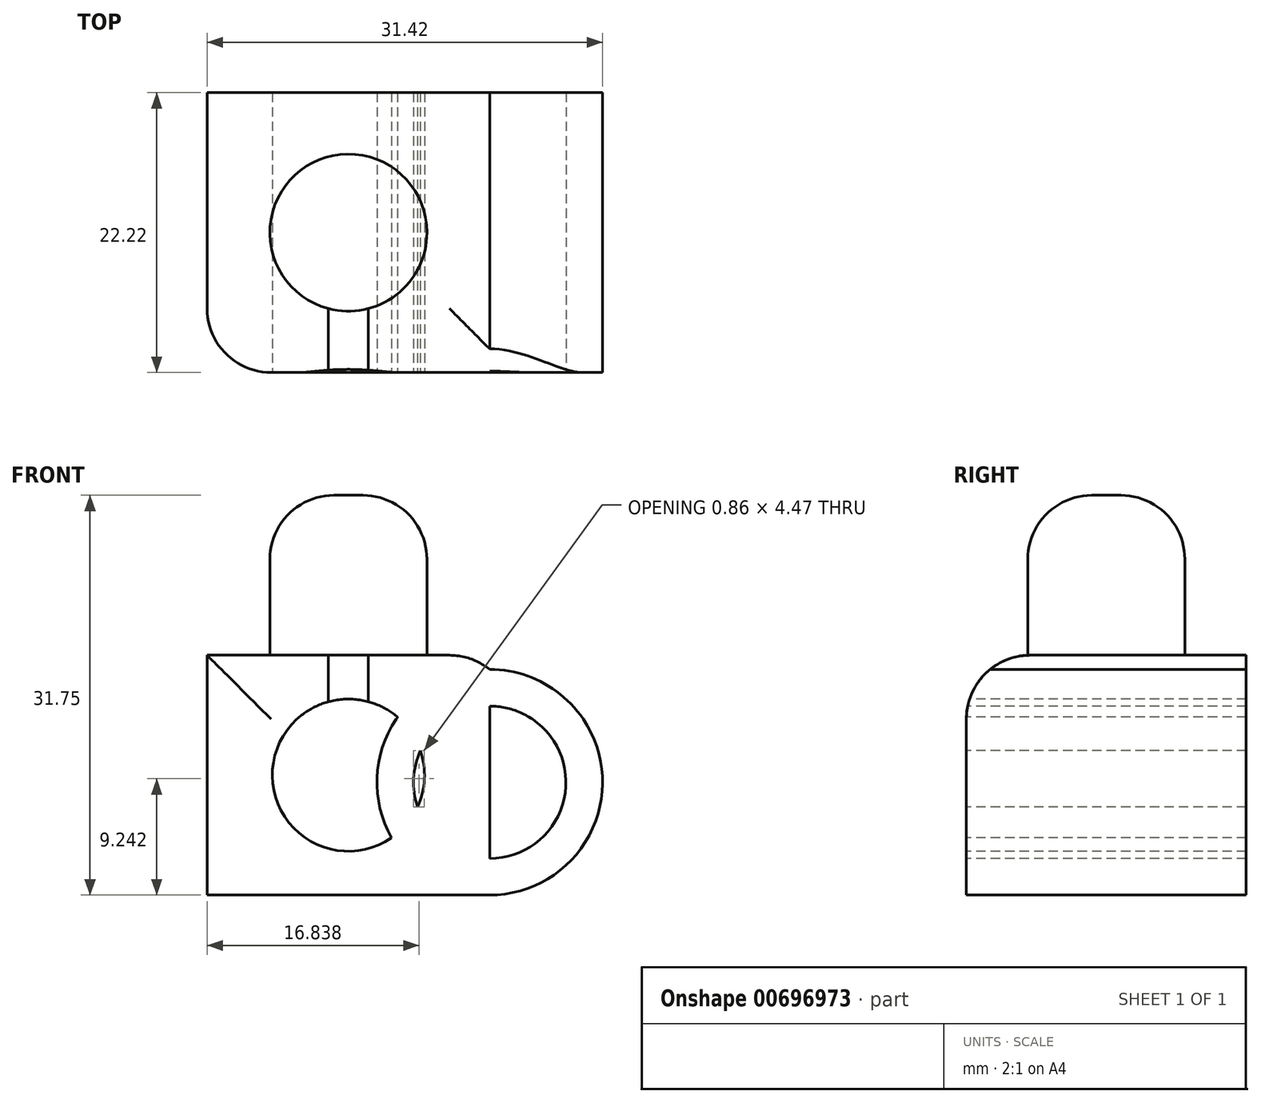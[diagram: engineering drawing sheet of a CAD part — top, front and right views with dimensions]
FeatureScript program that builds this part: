
annotation { "Feature Type Name" : "Feature", "Feature Type Description" : "" }
export const myFeature = defineFeature(function(context is Context, id is Id, definition is map)
    precondition{}
    {
        {
            var Q0;
            Q0=qCreatedBy(makeId("Top.planeOp"),FACE);
            var sketch = newSketch(context, id + "F0", { "sketchPlane" : qUnion([Q0])});
            skLineSegment(sketch, "E0.bottom", {"start": v(11.23, -11.11) * mm, "end": v(-11.23, -11.11) * mm});
            skLineSegment(sketch, "E0.top", {"start": v(11.23, 11.11) * mm, "end": v(-11.23, 11.11) * mm});
            skLineSegment(sketch, "E0.left", {"start": v(11.23, -11.11) * mm, "end": v(11.23, 11.11) * mm});
            skLineSegment(sketch, "E0.right", {"start": v(-11.23, -11.11) * mm, "end": v(-11.23, 11.11) * mm});
            skPoint(sketch, "E0.middle", {"position": v(0, 0) * mm});
            skSolve(sketch);
        }
        {
            var Q0;
            Q0=makeQuery(id+"F0.imprint","IMPRINT",FACE,{"disambiguationData":[TD([[makeQuery(id+"F0.imprint","IMPRINT",EDGE,{"derivedFrom":sQuery(id+"F0.wireOp",EDGE,"E0.bottom")}),-1.0]])]});
            extrude(context, id + "F1", {"entities" : qUnion([Q0]), "depth" : 19.05 * mm, "offsetDistance" : 25.4 * mm});
        }
        {
            var Q0;
            Q0=makeQuery(id+"F1.opExtrude","CAP_FACE",FACE,{"disambiguationData":[OSD([sQuery(id+"F0.wireOp",EDGE,"E0.bottom"),sQuery(id+"F0.wireOp",EDGE,"E0.top"),sQuery(id+"F0.wireOp",EDGE,"E0.left"),sQuery(id+"F0.wireOp",EDGE,"E0.right")])],"isStart":false});
            var sketch = newSketch(context, id + "F2", { "sketchPlane" : qUnion([Q0])});
            skCircle(sketch, "E1", {"center": v(0, 0) * mm, "radius": 6.24 * mm});
            skSolve(sketch);
        }
        {
            var Q0;
            Q0=makeQuery(id+"F2.imprint","IMPRINT",FACE,{"disambiguationData":[TD([[makeQuery(id+"F2.imprint","IMPRINT",EDGE,{"derivedFrom":sQuery(id+"F2.wireOp",EDGE,"E1")}),1.0]])]});
            extrude(context, id + "F3", {"entities" : qUnion([Q0]), "operationType" : NewBodyOperationType.ADD, "depth" : 12.7 * mm, "offsetDistance" : 25.4 * mm});
        }
        {
            var Q0;
            Q0=makeQuery(id+"F1.opExtrude","SWEPT_FACE",FACE,{"disambiguationData":[OSD([sQuery(id+"F0.wireOp",EDGE,"E0.bottom")])]});
            var sketch = newSketch(context, id + "F4", { "sketchPlane" : qUnion([Q0])});
            skCircle(sketch, "E2", {"center": v(0, 9.53) * mm, "radius": 6.04 * mm});
            skPoint(sketch, "E2.centerSnap0", {"position": v(-11.23, 9.53) * mm});
            skSolve(sketch);
        }
        {
            var Q0;
            Q0=makeQuery(id+"F4.imprint","IMPRINT",FACE,{"disambiguationData":[TD([[makeQuery(id+"F4.imprint","IMPRINT",EDGE,{"derivedFrom":sQuery(id+"F4.wireOp",EDGE,"E2")}),1.0]])]});
            extrude(context, id + "F5", {"entities" : qUnion([Q0]), "operationType" : NewBodyOperationType.REMOVE, "oppositeDirection" : true, "depth" : 25.4 * mm, "offsetDistance" : 25.4 * mm});
        }
        {
            var Q0;
            Q0=makeQuery(id+"F1.opExtrude","SWEPT_FACE",FACE,{"disambiguationData":[OSD([sQuery(id+"F0.wireOp",EDGE,"E0.left")])]});
            var sketch = newSketch(context, id + "F6", { "sketchPlane" : qUnion([Q0])});
            skLineSegment(sketch, "E3.bottom", {"start": v(11.11, 0) * mm, "end": v(-11.11, 0) * mm});
            skLineSegment(sketch, "E3.top", {"start": v(11.11, 2.9) * mm, "end": v(-11.11, 2.9) * mm});
            skLineSegment(sketch, "E3.left", {"start": v(11.11, 0) * mm, "end": v(11.11, 2.9) * mm});
            skLineSegment(sketch, "E3.right", {"start": v(-11.11, 0) * mm, "end": v(-11.11, 2.9) * mm});
            skPoint(sketch, "E3.middle", {"position": v(0, 1.45) * mm});
            skLineSegment(sketch, "E4", {"start": v(-11.11, 8.96) * mm, "end": v(11.11, 8.96) * mm});
            skSolve(sketch);
        }
        {
            var Q0;
            Q0=makeQuery(id+"F6.imprint","IMPRINT",FACE,{"disambiguationData":[TD([[makeQuery(id+"F6.imprint","IMPRINT",EDGE,{"derivedFrom":sQuery(id+"F6.wireOp",EDGE,"E3.bottom")}),1.0]])]});
            var Q1;
            Q1=sQuery(id+"F6.wireOp",EDGE,"E4");
            revolve(context, id + "F7", {"operationType" : NewBodyOperationType.ADD, "entities" : qUnion([Q0]), "axis" : qUnion([Q1]), "revolveType" : RevolveType.FULL});
        }
        {
            var Q0;
            Q0=makeQuery(id+"F1.opExtrude","CAP_EDGE",EDGE,{"disambiguationData":[OSD([sQuery(id+"F0.wireOp",EDGE,"E0.bottom")])],"isStart":false});
            var Q1;
            Q1=makeQuery(id+"F1.opExtrude","CAP_EDGE",EDGE,{"disambiguationData":[OSD([sQuery(id+"F0.wireOp",EDGE,"E0.left")])],"isStart":false});
            var Q2;
            Q2=makeQuery(id+"F3.opExtrude","CAP_EDGE",EDGE,{"disambiguationData":[OSD([sQuery(id+"F2.wireOp",EDGE,"E1")])],"isStart":false});
            var Q3;
            Q3=makeQuery(id+"F1.opExtrude","SWEPT_EDGE",EDGE,{"disambiguationData":[OSD([sQuery(id+"F0.wireOp",EDGE,"E0.bottom"),sQuery(id+"F0.wireOp",EDGE,"E0.right")])]});
            fillet(context, id + "F8", {"entities" : qUnion([Q0, Q1, Q2, Q3]), "radius" : 5.08 * mm, "tangentPropagation" : true, "allowEdgeOverflow" : false});
        }
    });
